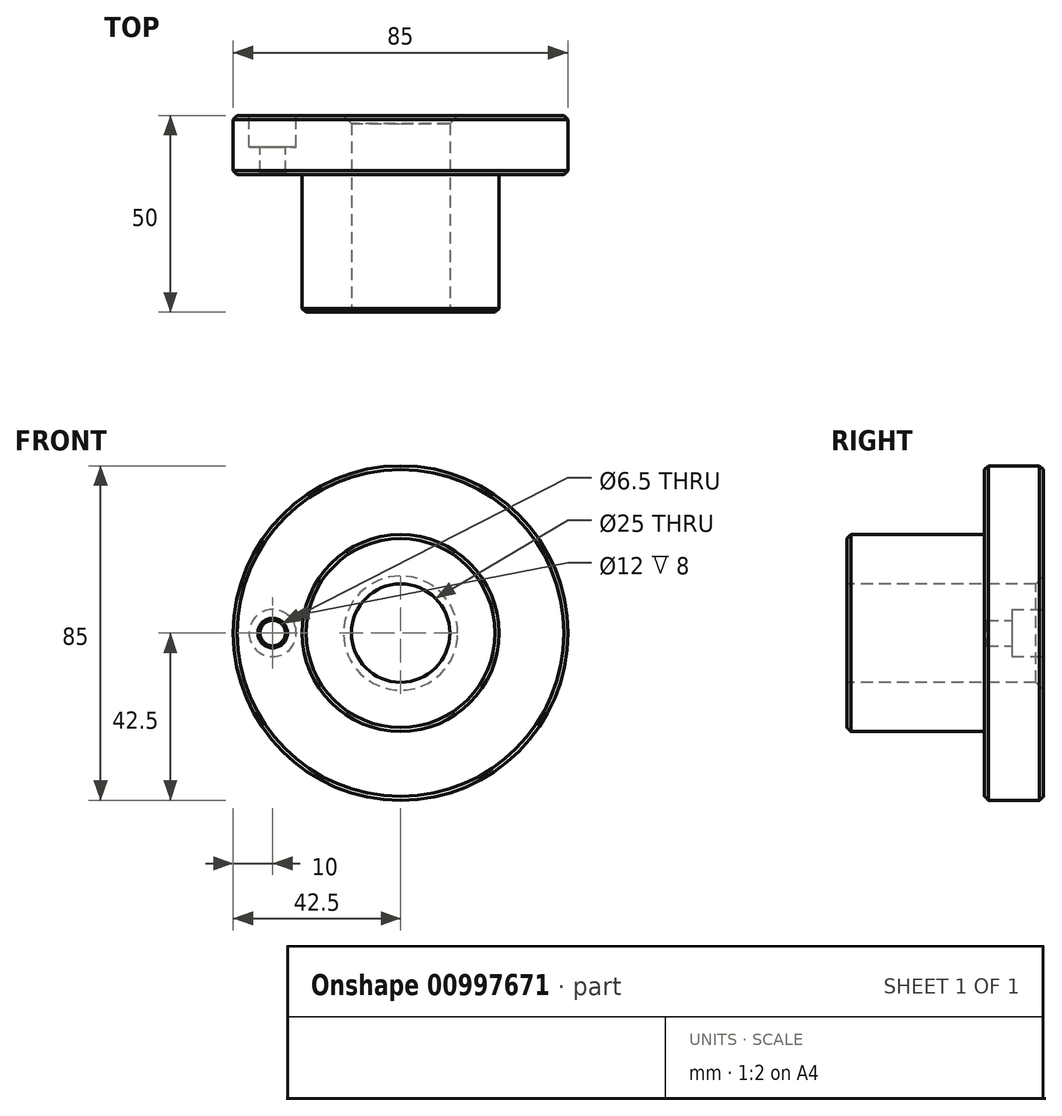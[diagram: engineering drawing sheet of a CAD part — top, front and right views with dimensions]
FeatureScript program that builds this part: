
annotation { "Feature Type Name" : "Feature", "Feature Type Description" : "" }
export const myFeature = defineFeature(function(context is Context, id is Id, definition is map)
    precondition{}
    {
        {
            var Q0;
            Q0=qCreatedBy(makeId("Front.planeOp"),FACE);
            var sketch = newSketch(context, id + "F0", { "sketchPlane" : qUnion([Q0])});
            skCircle(sketch, "E0", {"center": v(0, 0) * mm, "radius": 42.5 * mm});
            skCircle(sketch, "E1", {"center": v(0, 0) * mm, "radius": 25 * mm});
            skSolve(sketch);
        }
        {
            var Q0;
            Q0=makeQuery(id+"F0.imprint","IMPRINT",FACE,{"disambiguationData":[TD([[makeQuery(id+"F0.imprint","IMPRINT",EDGE,{"derivedFrom":sQuery(id+"F0.wireOp",EDGE,"E0")}),1.0]])]});
            var Q1;
            Q1=makeQuery(id+"F0.imprint","IMPRINT",FACE,{"disambiguationData":[TD([[makeQuery(id+"F0.imprint","IMPRINT",EDGE,{"derivedFrom":sQuery(id+"F0.wireOp",EDGE,"E1")}),1.0]])]});
            extrude(context, id + "F1", {"entities" : qUnion([Q0, Q1]), "depth" : 15 * mm, "offsetDistance" : 25 * mm});
        }
        {
            var Q0;
            Q0=makeQuery(id+"F0.imprint","IMPRINT",FACE,{"disambiguationData":[TD([[makeQuery(id+"F0.imprint","IMPRINT",EDGE,{"derivedFrom":sQuery(id+"F0.wireOp",EDGE,"E1")}),1.0]])]});
            extrude(context, id + "F2", {"entities" : qUnion([Q0]), "operationType" : NewBodyOperationType.ADD, "depth" : 50 * mm, "offsetDistance" : 25 * mm});
        }
        {
            var Q0;
            Q0=makeQuery(id+"F1.opExtrude","CAP_EDGE",EDGE,{"disambiguationData":[OSD([sQuery(id+"F0.wireOp",EDGE,"E0")])],"isStart":true});
            var Q1;
            Q1=makeQuery(id+"F1.opExtrude","CAP_EDGE",EDGE,{"disambiguationData":[OSD([sQuery(id+"F0.wireOp",EDGE,"E0")])],"isStart":false});
            var Q2;
            Q2=makeQuery(id+"F2.opExtrude","CAP_EDGE",EDGE,{"disambiguationData":[OSD([sQuery(id+"F0.wireOp",EDGE,"E1")])],"isStart":false});
            chamfer(context, id + "F3", {"entities" : qUnion([Q0, Q1, Q2]), "width" : 1 * mm, "tangentPropagation" : true});
        }
        {
            var Q0;
            Q0=makeQuery(id+"F2.opExtrude","CAP_FACE",FACE,{"disambiguationData":[OSD([sQuery(id+"F0.wireOp",EDGE,"E1")])],"isStart":false});
            var sketch = newSketch(context, id + "F4", { "sketchPlane" : qUnion([Q0])});
            skCircle(sketch, "E2", {"center": v(0, 0) * mm, "radius": 12.5 * mm});
            skSolve(sketch);
        }
        {
            var Q0;
            Q0=makeQuery(id+"F4.imprint","IMPRINT",FACE,{"disambiguationData":[TD([[makeQuery(id+"F4.imprint","IMPRINT",EDGE,{"derivedFrom":sQuery(id+"F4.wireOp",EDGE,"E2")}),1.0]])]});
            extrude(context, id + "F5", {"entities" : qUnion([Q0]), "operationType" : NewBodyOperationType.REMOVE, "endBound" : BoundingType.THROUGH_ALL, "oppositeDirection" : true, "depth" : 25 * mm, "offsetDistance" : 25 * mm});
        }
        {
            var Q0;
            Q0=makeQuery(id+"F5.boolean.opBoolean","COPY",EDGE,{"derivedFrom":makeQuery(id+"F5.opExtrude","CAP_EDGE",EDGE,{"disambiguationData":[OSD([sQuery(id+"F4.wireOp",EDGE,"E2")])],"isStart":true})});
            var Q1;
            Q1=makeQuery(id+"F5.boolean.opBoolean","INTERSECT",EDGE,{"derivedFrom":[makeQuery(id+"F1.opExtrude","CAP_FACE",FACE,{"disambiguationData":[OSD([sQuery(id+"F0.wireOp",EDGE,"E0")])],"isStart":true}),makeQuery(id+"F5.opExtrude","SWEPT_FACE",FACE,{"disambiguationData":[OSD([sQuery(id+"F4.wireOp",EDGE,"E2")])]})]});
            chamfer(context, id + "F6", {"entities" : qUnion([Q0, Q1]), "width" : 2 * mm, "tangentPropagation" : true});
        }
        {
            var Q0;
            Q0=makeQuery(id+"F1.opExtrude","CAP_FACE",FACE,{"disambiguationData":[OSD([sQuery(id+"F0.wireOp",EDGE,"E0")])],"isStart":true});
            var sketch = newSketch(context, id + "F7", { "sketchPlane" : qUnion([Q0])});
            skCircle(sketch, "E3", {"center": v(0, 0) * mm, "radius": 32.5 * mm, "construction": true});
            skLineSegment(sketch, "E4", {"start": v(48.8, 0) * mm, "end": v(0, 0) * mm, "construction": true});
            skCircle(sketch, "E5", {"center": v(32.5, 0) * mm, "radius": 6 * mm});
            skCircle(sketch, "E6", {"center": v(32.5, 0) * mm, "radius": 3.25 * mm});
            skSolve(sketch);
        }
        {
            var Q0;
            Q0=makeQuery(id+"F7.imprint","IMPRINT",FACE,{"disambiguationData":[TD([[makeQuery(id+"F7.imprint","IMPRINT",EDGE,{"derivedFrom":sQuery(id+"F7.wireOp",EDGE,"E6")}),1.0]])]});
            extrude(context, id + "F8", {"entities" : qUnion([Q0]), "operationType" : NewBodyOperationType.REMOVE, "endBound" : BoundingType.THROUGH_ALL, "oppositeDirection" : true, "depth" : 25 * mm, "offsetDistance" : 25 * mm});
        }
        {
            var Q0;
            Q0=makeQuery(id+"F7.imprint","IMPRINT",FACE,{"disambiguationData":[TD([[makeQuery(id+"F7.imprint","IMPRINT",EDGE,{"derivedFrom":sQuery(id+"F7.wireOp",EDGE,"E5")}),1.0]])]});
            extrude(context, id + "F9", {"entities" : qUnion([Q0]), "operationType" : NewBodyOperationType.REMOVE, "oppositeDirection" : true, "depth" : 8 * mm, "offsetDistance" : 25 * mm});
        }
        {
            var Q0;
            Q0=makeQuery(id+"F9.boolean.opBoolean","COPY",EDGE,{"derivedFrom":makeQuery(id+"F9.opExtrude","CAP_EDGE",EDGE,{"disambiguationData":[OSD([sQuery(id+"F7.wireOp",EDGE,"E5")])],"isStart":true})});
            var Q1;
            Q1=makeQuery(id+"F8.boolean.opBoolean","INTERSECT",EDGE,{"derivedFrom":[makeQuery(id+"F1.opExtrude","CAP_FACE",FACE,{"disambiguationData":[OSD([sQuery(id+"F0.wireOp",EDGE,"E0")])],"isStart":false}),makeQuery(id+"F8.opExtrude","SWEPT_FACE",FACE,{"disambiguationData":[OSD([sQuery(id+"F7.wireOp",EDGE,"E6")])]})]});
            chamfer(context, id + "F10", {"entities" : qUnion([Q0, Q1]), "width" : 0.5 * mm, "tangentPropagation" : true});
        }
    });
